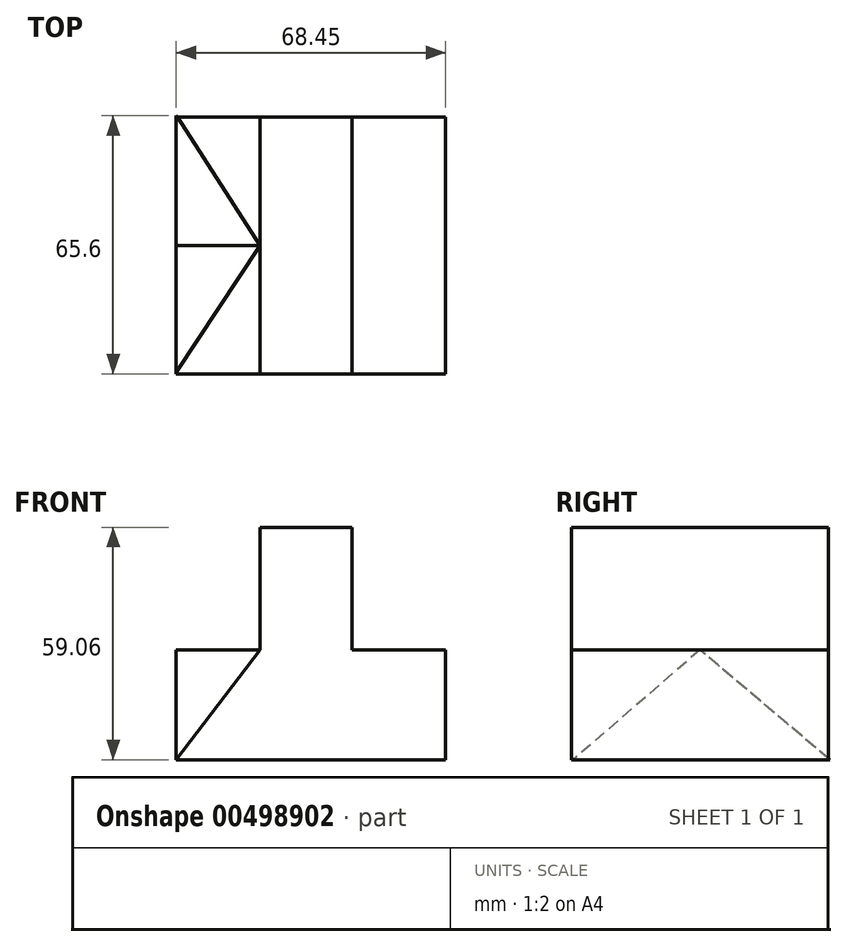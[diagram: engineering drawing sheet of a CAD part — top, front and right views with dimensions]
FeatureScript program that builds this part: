
annotation { "Feature Type Name" : "Feature", "Feature Type Description" : "" }
export const myFeature = defineFeature(function(context is Context, id is Id, definition is map)
    precondition{}
    {
        {
            var Q0;
            Q0=qCreatedBy(makeId("Front.planeOp"),FACE);
            var sketch = newSketch(context, id + "F0", { "sketchPlane" : qUnion([Q0])});
            skLineSegment(sketch, "E0", {"start": v(0, 0) * mm, "end": v(68.45, 0) * mm});
            skLineSegment(sketch, "E1", {"start": v(68.45, 0) * mm, "end": v(68.45, 27.93) * mm});
            skLineSegment(sketch, "E2", {"start": v(68.45, 27.93) * mm, "end": v(44.64, 27.93) * mm});
            skLineSegment(sketch, "E3", {"start": v(44.64, 27.93) * mm, "end": v(44.64, 59.06) * mm});
            skLineSegment(sketch, "E4", {"start": v(44.64, 59.06) * mm, "end": v(21.29, 59.06) * mm});
            skLineSegment(sketch, "E5", {"start": v(21.29, 59.06) * mm, "end": v(21.29, 27.93) * mm});
            skLineSegment(sketch, "E6", {"start": v(21.29, 27.93) * mm, "end": v(0, 0) * mm});
            skSolve(sketch);
        }
        {
            var Q0;
            Q0=makeQuery(id+"F0.imprint","IMPRINT",FACE,{"disambiguationData":[TD([[makeQuery(id+"F0.imprint","IMPRINT",EDGE,{"derivedFrom":sQuery(id+"F0.wireOp",EDGE,"E0")}),1.0]])]});
            extrude(context, id + "F1", {"entities" : qUnion([Q0]), "endBound" : BoundingType.SYMMETRIC, "depth" : 65.2 * mm});
        }
        {
            var Q0;
            Q0=qCreatedBy(makeId("Right.planeOp"),FACE);
            var sketch = newSketch(context, id + "F2", { "sketchPlane" : qUnion([Q0])});
            skLineSegment(sketch, "E7.0", {"start": v(-32.6, 27.93) * mm, "end": v(32.6, 27.93) * mm, "construction": true});
            skLineSegment(sketch, "E8", {"start": v(33, 0) * mm, "end": v(0, 27.93) * mm});
            skLineSegment(sketch, "E9", {"start": v(0, 27.93) * mm, "end": v(-32.26, 0) * mm});
            skLineSegment(sketch, "E10", {"start": v(-32.26, 0) * mm, "end": v(33, 0) * mm});
            skSolve(sketch);
        }
        {
            var Q0;
            Q0=makeQuery(id+"F2.imprint","IMPRINT",FACE,{"disambiguationData":[TD([[makeQuery(id+"F2.imprint","IMPRINT",EDGE,{"derivedFrom":sQuery(id+"F2.wireOp",EDGE,"E8")}),1.0]])]});
            var Q1;
            Q1=makeQuery(id+"F1.opExtrude","SWEPT_FACE",FACE,{"disambiguationData":[OSD([sQuery(id+"F0.wireOp",EDGE,"E6")])]});
            extrude(context, id + "F3", {"entities" : qUnion([Q0]), "operationType" : NewBodyOperationType.ADD, "endBound" : BoundingType.UP_TO_SURFACE, "endBoundEntityFace" : qUnion([Q1]), "depth" : 25 * mm});
        }
    });
